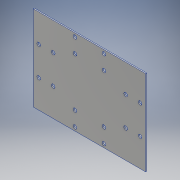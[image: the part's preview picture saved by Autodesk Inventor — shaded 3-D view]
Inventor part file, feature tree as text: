
AUTODESK INVENTOR PART (.ipt)
format: ipt  version: 2018.1 (Build 221171000, 171)  size: 133,120 bytes
history: native  units: mm
features: extrude x2, sketch x2, other x1
ambient origin geometry x8: Origin, YZ Plane, XZ Plane, XY Plane, X Axis, Y Axis, Z Axis, Center Point
bodies: Body1 (feature_tree)
feature tree (5):
  other  "ソリッド1"
  extrude  "押し出し1"  Depth=310.0mm
  extrude  "押し出し2"  Depth=235.0mm
  sketch  "スケッチ1"
  sketch  "スケッチ2"
